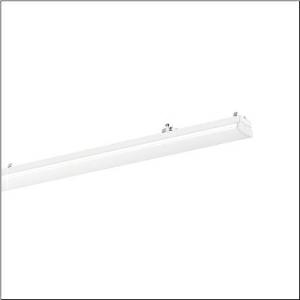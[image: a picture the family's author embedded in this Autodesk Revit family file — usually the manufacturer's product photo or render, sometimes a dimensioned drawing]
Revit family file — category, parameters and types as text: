
# Revit family: licross_21_recessed_opal_mo_52te1ddn495g
name_source: partatom
category: Lighting Fixtures
units: mm (PartAtom-declared; Revit-internal decimal feet)

## family parameters
Cut with Voids When Loaded = No
Host = Face
Light Source = No
Part Type = Normal
Room Calculation Point = No
Round Connector Dimension = Use Diameter
Shared = No

## types (1)
- --- (1 x LED, 9740 lm, 58 W, 4000K)
    Apparent Load = 58 VA
    CIE Flux Codes = 44 73 91 87 100
    Color Rendering = 80
    Color Temperature = 4000K
    Default Elevation = 1800 mm
    Description = Licross 21 recessed opal MO, luminaire insert, of sheet steel, galvanised, coil coated, white, length: 1.500mm, width: 66mm, height: 67mm, LED rated luminous flux: 9.750lm, light colour: 840, SDCM (Standard Deviation of Colour Matching)MacAdam ≤ 3 SDCM (initial), control gear: DALI 2, with plug, 5-pole, with phase selection, mains connection: 220..240V, AC, 50/60Hz, rated input power: 58W, internal wiring halogen-free, primary optical cover: cover, of PMMA, light emission: direct with ceiling illumination distribution, primary light characteristic: symmetric, protection rating (complete): IP54, insulation class (complete): insulation class I (protective earthing), certification: CE, ENEC, VDE, UKCA, protection symbol: D if used in an environment with non-conductive dust loads with corresponding accessories, impact resistance: IK06, permissible ambient temperature for indoor applications: -25..+35°C, corresponds to IFS (International Featured Standards) requirements for safety and quality in the food industry, reducing of maximum allowable ambient temperature of 5°C with ceiling mounting, LABS conformity tested according to VDMA 24364:2018-05, The light source and the operating device comply with the requirements of the Ecodesign Regulation (EU) 2019/2020 and are replaceable in accordance with this regulation, packaging unit: 1 piece
    Height = 83 mm
    Lamp = 1 x LED
    Lamp Light Flux = 9740 lm
    Lamp Power = 58 W
    Lamp count = 1
    Length = 1500 mm
    Luminous efficacy = 168 lm/W
    Manufacturer = Siteco
    ModVariant = No
    Model = 52TE1DDN495G
    Mounting Place = Ceiling
    Mounting Type = Pendant
    Number of Poles = 1
    OnlyDefault = Yes
    Power Factor = 1
    Product Name = Licross 21 recessed opal MO
    Product group = luminaire insert | ceiling pendant
    ProductGroupID = 901
    Protection Class = Protection class I
    Protection Degree = IP 54
    RLX_Detail_Level = 1
    RLX_Emergency_Light_Flux = 0 lm
    RLX_Emergency_Type = 0
    RLX_Emergency_Type_DB = No
    RlxData = <blob elided: 27221 chars, md5=80b7c641>
    Socket = socket
    Standby Power = 0 W
    System Light Flux = 9740 lm
    System Power = 58 W
    Type Comments = factory setting: luminous flux: 100 % | dim-lin: 254 | 390 mA
    Type Image = l_1313666.jpg
    URL = http://relux.com
    VarID = @adj_076245
    Voltage = 0 V
    Weight = 0.00 kg
    Width = 76 mm

## geometry (parser evidence)
native form markers: Blend x4, Sweep x14
no freeform markers — native parametric forms only
